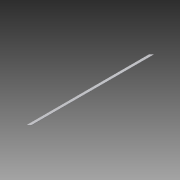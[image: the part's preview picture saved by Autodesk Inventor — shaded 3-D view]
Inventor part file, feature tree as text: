
AUTODESK INVENTOR PART (.ipt)
format: ipt  version: 2015 SP1 (Build 190203100, 203)  size: 98,304 bytes
history: native  units: in
note: dims shown in document units (in); Inventor stores cm internally (conversion verified against a paired STEP export)
features: sketch x2, extrude x1, hole x1, projected_geometry x1
ambient origin geometry x8: Origin, YZ Plane, XZ Plane, XY Plane, X Axis, Y Axis, Z Axis, Center Point
bodies: Solid1 (feature_tree)
feature tree (5):
  extrude  "Extrusion1"  Depth=0.125in
  hole  "Hole1"  [1 undecoded]
  sketch  "Sketch1"  dims[d0=1.0in d1=0.125in]
  sketch  "Sketch2"  dims[d2=66.5in d3=0.0in d4=0.5in d5=0.5in d6=0.5in d7=1.0in d8=0.25in d9=0.75in d10=0.375in d11=0.25in d12=0.5635in d13=1.0in d14=0.8108in]
  projected_geometry  "Projected Loop1"
note: 1 required parameter value undecoded (feature->parameter linkage not recoverable at this tier; creation-order binding heuristic only, values carry confidence <= 0.55)
